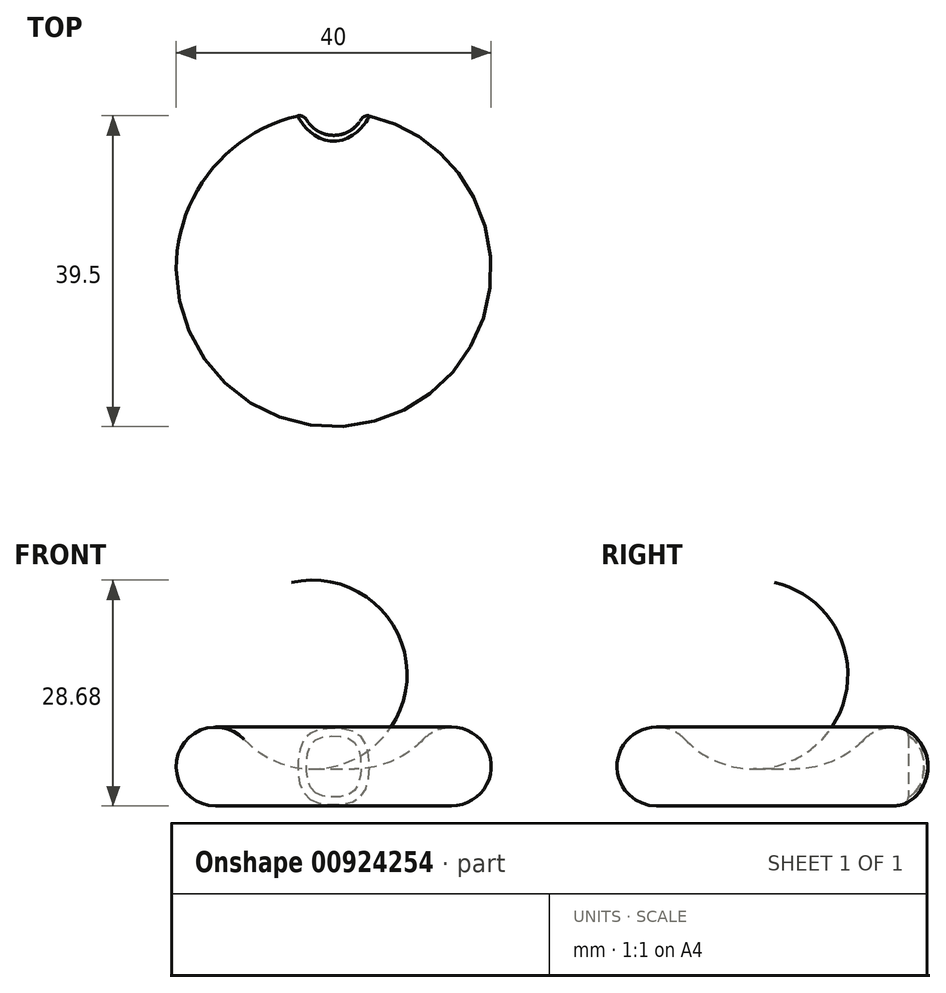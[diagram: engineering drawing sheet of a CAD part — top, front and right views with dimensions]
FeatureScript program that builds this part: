
annotation { "Feature Type Name" : "Feature", "Feature Type Description" : "" }
export const myFeature = defineFeature(function(context is Context, id is Id, definition is map)
    precondition{}
    {
        {
            var Q0;
            Q0=qCreatedBy(makeId("Front.planeOp"),FACE);
            var sketch = newSketch(context, id + "F0", { "sketchPlane" : qUnion([Q0])});
            skArc(sketch, "E0", {"start": v(-11.37, 8.44) * mm, "mid": v(-19.6, 6.97) * mm, "end": v(-15, 0) * mm});
            skArc(sketch, "E1", {"start": v(-11.37, 8.44) * mm, "mid": v(-6.14, 5.21) * mm, "end": v(0, 5) * mm});
            skLineSegment(sketch, "E2", {"start": v(-15, 0) * mm, "end": v(0, 0) * mm});
            skLineSegment(sketch, "E3", {"start": v(0, 0) * mm, "end": v(0, 5) * mm});
            skSolve(sketch);
        }
        {
            var Q0;
            Q0=makeQuery(id+"F0.imprint","IMPRINT",FACE,{"disambiguationData":[TD([[makeQuery(id+"F0.imprint","IMPRINT",EDGE,{"derivedFrom":sQuery(id+"F0.wireOp",EDGE,"E0")}),1.0]])]});
            var Q1;
            Q1=sQuery(id+"F0.wireOp",EDGE,"E3");
            revolve(context, id + "F1", {"surfaceOperationType" : NewSurfaceOperationType.NEW, "entities" : qUnion([Q0]), "axis" : qUnion([Q1]), "revolveType" : RevolveType.FULL});
        }
        {
            var Q0;
            Q0=qCreatedBy(makeId("Top.planeOp"),FACE);
            var sketch = newSketch(context, id + "F2", { "sketchPlane" : qUnion([Q0])});
            skCircle(sketch, "E4", {"center": v(0, 21) * mm, "radius": 4 * mm});
            skSolve(sketch);
        }
        {
            var Q0;
            Q0=makeQuery(id+"F2.imprint","IMPRINT",FACE,{"disambiguationData":[TD([[makeQuery(id+"F2.imprint","IMPRINT",EDGE,{"derivedFrom":sQuery(id+"F2.wireOp",EDGE,"E4")}),1.0]])]});
            extrude(context, id + "F3", {"entities" : qUnion([Q0]), "operationType" : NewBodyOperationType.REMOVE, "depth" : 25.4 * mm, "offsetDistance" : 25.4 * mm});
        }
        {
            var Q0;
            Q0=makeQuery(id+"F3.boolean.opBoolean","COPY",FACE,{"derivedFrom":makeQuery(id+"F3.opExtrude","SWEPT_FACE",FACE,{"disambiguationData":[OSD([sQuery(id+"F2.wireOp",EDGE,"E4")])]})});
            fillet(context, id + "F4", {"entities" : qUnion([Q0]), "radius" : 1 * mm, "tangentPropagation" : true, "allowEdgeOverflow" : false});
        }
    });
